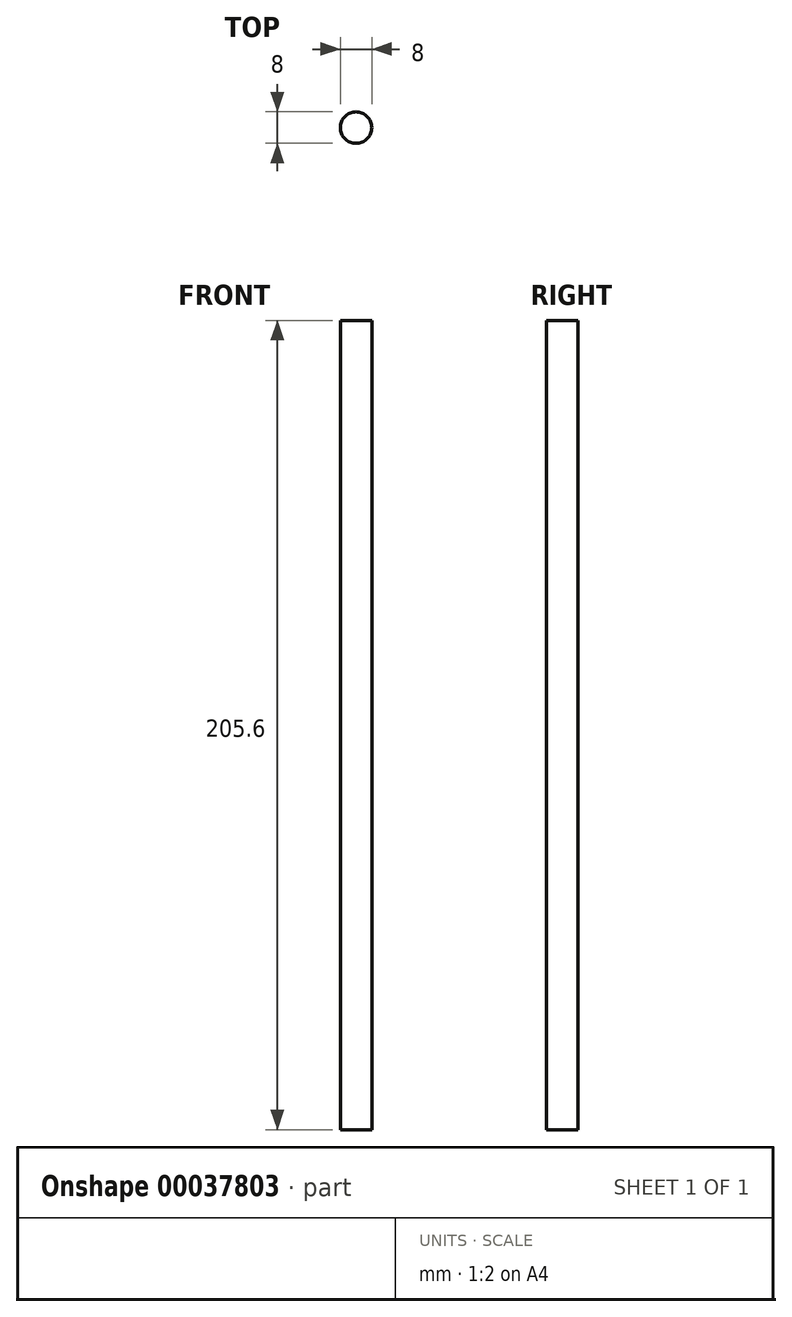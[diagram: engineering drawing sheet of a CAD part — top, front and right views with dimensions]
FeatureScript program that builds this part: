
annotation { "Feature Type Name" : "Feature", "Feature Type Description" : "" }
export const myFeature = defineFeature(function(context is Context, id is Id, definition is map)
    precondition{}
    {
        {
            var Q0;
            Q0=qCreatedBy(makeId("Top.planeOp"),FACE);
            var sketch = newSketch(context, id + "F0", { "sketchPlane" : qUnion([Q0])});
            skCircle(sketch, "E0", {"center": v(0, 0) * mm, "radius": 4 * mm});
            skSolve(sketch);
        }
        {
            var Q0;
            Q0 = qSketchRegion(id + "F0", true);
            extrude(context, id + "F1", {"entities" : qUnion([Q0]), "depth" : 205.6 * mm});
        }
    });
